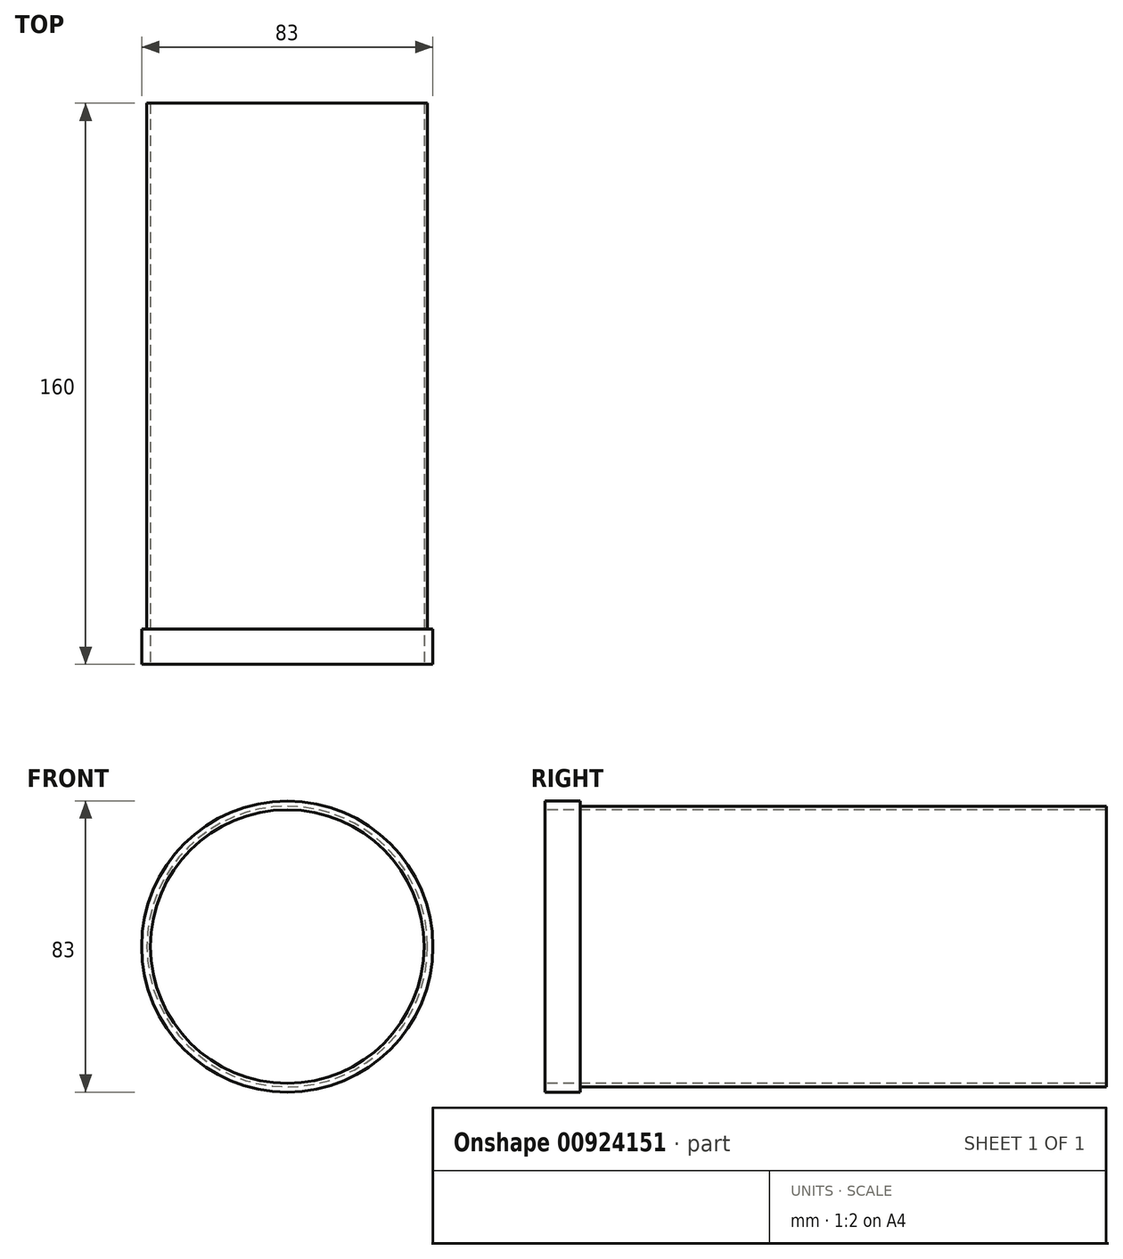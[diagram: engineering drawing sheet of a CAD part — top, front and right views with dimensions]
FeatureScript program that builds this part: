
annotation { "Feature Type Name" : "Feature", "Feature Type Description" : "" }
export const myFeature = defineFeature(function(context is Context, id is Id, definition is map)
    precondition{}
    {
        {
            var Q0;
            Q0=qCreatedBy(makeId("Front.planeOp"),FACE);
            var sketch = newSketch(context, id + "F0", { "sketchPlane" : qUnion([Q0])});
            skCircle(sketch, "E0", {"center": v(0, 0) * mm, "radius": 40 * mm});
            skCircle(sketch, "E1", {"center": v(0, 0) * mm, "radius": 39 * mm});
            skSolve(sketch);
        }
        {
            var Q0;
            Q0 = qSketchRegion(id + "F0", true);
            extrude(context, id + "F1", {"entities" : qUnion([Q0]), "oppositeDirection" : true, "depth" : 150 * mm, "offsetDistance" : 25 * mm});
        }
        {
            var Q0;
            Q0=makeQuery(id+"F1.opExtrude","CAP_FACE",FACE,{"disambiguationData":[OSD([sQuery(id+"F0.wireOp",EDGE,"E0"),sQuery(id+"F0.wireOp",EDGE,"E1")])],"isStart":true});
            var sketch = newSketch(context, id + "F2", { "sketchPlane" : qUnion([Q0])});
            skCircle(sketch, "E2", {"center": v(0, 0) * mm, "radius": 39 * mm});
            skCircle(sketch, "E3", {"center": v(0, 0) * mm, "radius": 41.5 * mm});
            skSolve(sketch);
        }
        {
            var Q0;
            Q0 = qSketchRegion(id + "F2", true);
            extrude(context, id + "F3", {"entities" : qUnion([Q0]), "operationType" : NewBodyOperationType.ADD, "depth" : 10 * mm, "offsetDistance" : 25 * mm});
        }
    });
